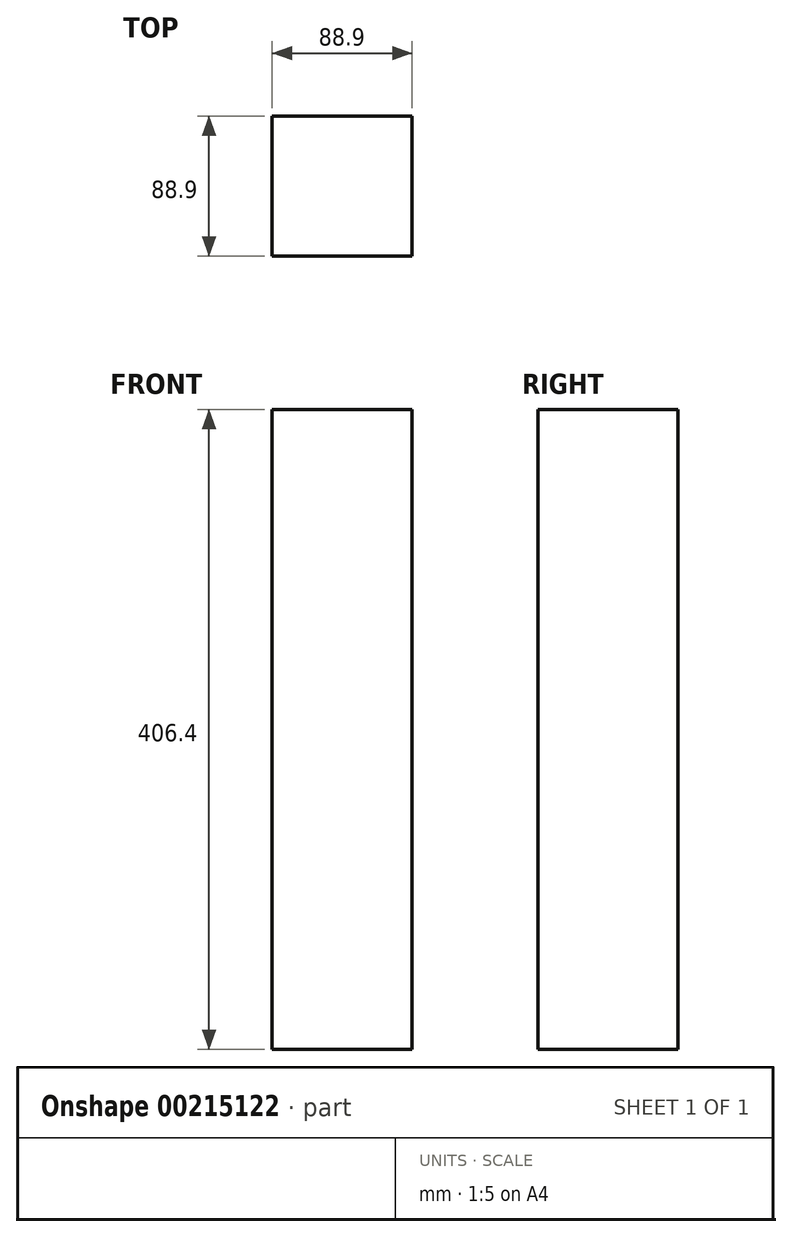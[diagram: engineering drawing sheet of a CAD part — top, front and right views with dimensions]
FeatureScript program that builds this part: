
annotation { "Feature Type Name" : "Feature", "Feature Type Description" : "" }
export const myFeature = defineFeature(function(context is Context, id is Id, definition is map)
    precondition{}
    {
        {
            var Q0;
            Q0=qCreatedBy(makeId("Top.planeOp"),FACE);
            var sketch = newSketch(context, id + "F0", { "sketchPlane" : qUnion([Q0])});
            skLineSegment(sketch, "E0.bottom", {"start": v(0, 0) * mm, "end": v(88.9, 0) * mm});
            skLineSegment(sketch, "E0.top", {"start": v(0, 88.9) * mm, "end": v(88.9, 88.9) * mm});
            skLineSegment(sketch, "E0.left", {"start": v(0, 0) * mm, "end": v(0, 88.9) * mm});
            skLineSegment(sketch, "E0.right", {"start": v(88.9, 0) * mm, "end": v(88.9, 88.9) * mm});
            skSolve(sketch);
        }
        {
            var Q0;
            Q0=makeQuery(id+"F0.imprint","IMPRINT",FACE,{"disambiguationData":[TD([[makeQuery(id+"F0.imprint","IMPRINT",EDGE,{"derivedFrom":sQuery(id+"F0.wireOp",EDGE,"E0.bottom")}),1.0]])]});
            extrude(context, id + "F1", {"entities" : qUnion([Q0]), "depth" : 406.4 * mm, "offsetDistance" : 25.4 * mm});
        }
    });
